# Revit family: Toilet-Floor_Mount-KOHLER-OVE-K-17629T.rfa_
name_source: partatom
category: Plumbing Fixtures
units: mm (PartAtom-declared; Revit-internal decimal feet)

## family parameters
Cut with Voids When Loaded = No
Host = Face
OmniClass Number = 23.31.19.00
OmniClass Title = Toilets
Part Type = Normal
Room Calculation Point = No
Round Connector Dimension = Use Diameter
Shared = No

## types (3) — shared parameters
ADA Compliant = No
Assembly Code = D2010100
Bowl Height = 15 9/16"
CW Connection = Yes
Cold Water Inlet = Cold Water Inlet
Date Modified = 06/13/2024
Default Elevation = 0"
Description = One-piece Toilet With Quiet Close Seat
Finish = Kohler-Vitreous_China-0-White
Flow Rate = 0 GPM
Flush Rate- GPF = 1.5GPF
Flush Rate- LPF = 6 LPF
HW Connection = No
Height = 27 9/16"
Hot Water Inlet = Hot Water Inlet
Length = 29 1/16"
Manufacturer = Kohler Co.
Master Format 2014 = 22 42 13.13
Master Format 2014 Name = Residential Water Closets
Material = Vitreous China
Pressure = 0.00 psi
Product Name = Ove
Rough-In P-Trap = 7 1/8"
Rough-In S-Trap = 12"
URL = http://www.kohler.com.cn
Vent Connection = No
Waste Connection = Yes
Waste Water Outlet = Waste Water Outlet
WaterSense Certified = No
Width = 14 3/4"

## per-type parameters (varying)
| type | Model | P-Trap | Product Documentation Link | Product Page URL | Seat Included | Type |
| S-Trap, 0-White | K-17629T-S2-0 | No | https://files.kohler.com.cn | https://www.kohler.com.cn | Yes | 1 |
| P-Trap With Seat, 0-White | K-17629T-ZY-0 | Yes |  |  | Yes | 2 |
| S-Trap Without Seat, 0-White | K-17629T-NS-0 | No |  |  | No | 3 |

## geometry (parser evidence)
native form markers: Sweep x7
no freeform markers — native parametric forms only
